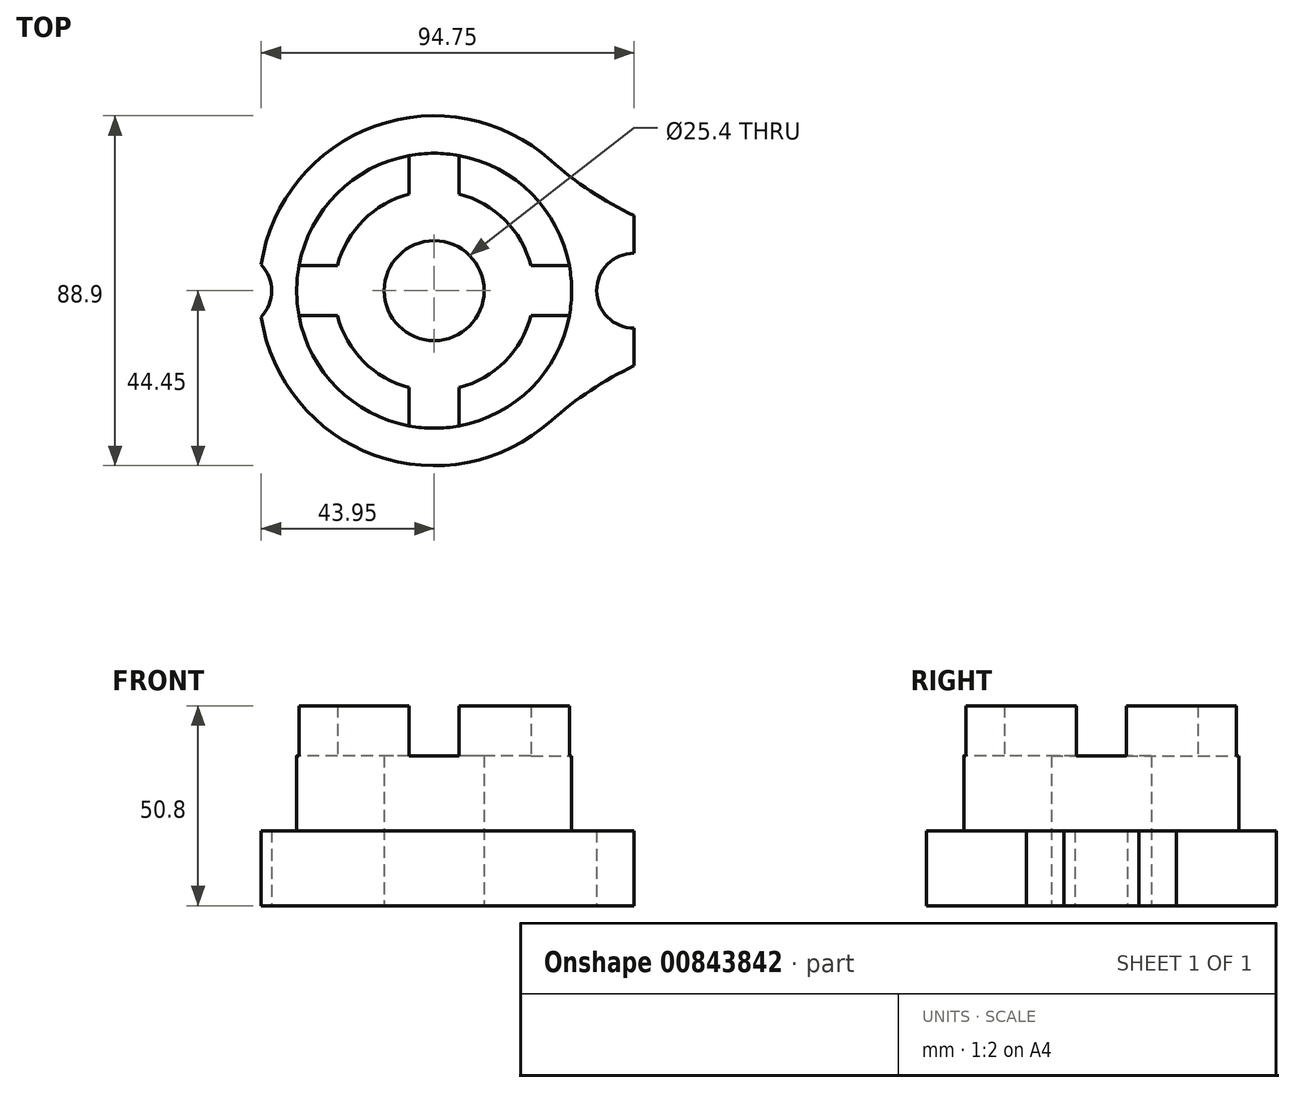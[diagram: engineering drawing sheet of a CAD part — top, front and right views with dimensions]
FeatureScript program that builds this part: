
annotation { "Feature Type Name" : "Feature", "Feature Type Description" : "" }
export const myFeature = defineFeature(function(context is Context, id is Id, definition is map)
    precondition{}
    {
        {
            var Q0;
            Q0=qCreatedBy(makeId("Top.planeOp"),FACE);
            var sketch = newSketch(context, id + "F0", { "sketchPlane" : qUnion([Q0])});
            skCircle(sketch, "E0", {"center": v(0, 0) * mm, "radius": 12.7 * mm});
            skCircle(sketch, "E1", {"center": v(0, 0) * mm, "radius": 25.4 * mm});
            skCircle(sketch, "E2", {"center": v(0, 0) * mm, "radius": 34.93 * mm});
            skLineSegment(sketch, "E3.top", {"start": v(0, -50.8) * mm, "end": v(50.8, -50.8) * mm});
            skLineSegment(sketch, "E4.top", {"start": v(0, 50.8) * mm, "end": v(50.8, 50.8) * mm});
            skLineSegment(sketch, "E5.bottom", {"start": v(50.8, 50.8) * mm, "end": v(-50.8, 50.8) * mm});
            skLineSegment(sketch, "E5.top", {"start": v(50.8, -50.8) * mm, "end": v(-50.8, -50.8) * mm});
            skLineSegment(sketch, "E5.right", {"start": v(-50.8, 50.8) * mm, "end": v(-50.8, -50.8) * mm});
            skLineSegment(sketch, "E6", {"start": v(50.8, 50.8) * mm, "end": v(50.8, -50.8) * mm});
            skLineSegment(sketch, "E7", {"start": v(-6.35, -24.6) * mm, "end": v(-6.35, -34.34) * mm});
            skLineSegment(sketch, "E8", {"start": v(6.35, -24.6) * mm, "end": v(6.35, -34.34) * mm});
            skLineSegment(sketch, "E9", {"start": v(24.6, -6.35) * mm, "end": v(34.34, -6.35) * mm});
            skLineSegment(sketch, "E10", {"start": v(24.6, 6.35) * mm, "end": v(34.34, 6.35) * mm});
            skLineSegment(sketch, "E11", {"start": v(-6.35, 24.6) * mm, "end": v(-6.35, 34.34) * mm});
            skLineSegment(sketch, "E12", {"start": v(6.35, 24.6) * mm, "end": v(6.35, 34.34) * mm});
            skLineSegment(sketch, "E13", {"start": v(-24.6, 6.35) * mm, "end": v(-34.34, 6.35) * mm});
            skLineSegment(sketch, "E14", {"start": v(-24.6, -6.35) * mm, "end": v(-34.34, -6.35) * mm});
            skCircle(sketch, "E15", {"center": v(50.8, 0) * mm, "radius": 9.53 * mm});
            skCircle(sketch, "E16", {"center": v(-50.8, 0) * mm, "radius": 9.53 * mm});
            skCircle(sketch, "E17", {"center": v(0, 0) * mm, "radius": 44.45 * mm});
            skCircle(sketch, "E18", {"center": v(-50.8, 0) * mm, "radius": 19.05 * mm});
            skCircle(sketch, "E19", {"center": v(50.8, 0) * mm, "radius": 19.05 * mm});
            skSolve(sketch);
        }
        {
            var Q0;
            {var subQ0=sQuery(id+"F0.wireOp",EDGE,"E5.right");var subQ1=sQuery(id+"F0.wireOp",EDGE,"E16");var subQ2=makeQuery(id+"F0.imprint","INTERSECT",VERTEX,{"disambiguationData":[OD(1.0)],"derivedFrom":[subQ1,subQ0]});Q0=makeQuery(id+"F0.imprint","IMPRINT",FACE,{"disambiguationData":[TD([[makeQuery(id+"F0.imprint","IMPRINT",EDGE,{"disambiguationData":[TD([[subQ2,-1.0]])],"derivedFrom":subQ1}),-1.0]])]});}
            var Q1;
            {var subQ5=sQuery(id+"F0.wireOp",EDGE,"E2");var subQ8=makeQuery(id+"F0.imprint","INTERSECT",VERTEX,{"derivedFrom":[subQ5,sQuery(id+"F0.wireOp",EDGE,"E7")]});Q1=makeQuery(id+"F0.imprint","IMPRINT",FACE,{"disambiguationData":[TD([[makeQuery(id+"F0.imprint","IMPRINT",EDGE,{"disambiguationData":[TD([[subQ8,1.0]])],"derivedFrom":subQ5}),-1.0]])]});}
            var Q2;
            {var subQ7=sQuery(id+"F0.wireOp",EDGE,"E12");Q2=makeQuery(id+"F0.imprint","IMPRINT",FACE,{"disambiguationData":[TD([[makeQuery(id+"F0.imprint","IMPRINT",EDGE,{"derivedFrom":subQ7}),-1.0]])]});}
            var Q3;
            {var subQ0=sQuery(id+"F0.wireOp",EDGE,"E17");var subQ1=sQuery(id+"F0.wireOp",EDGE,"E15");var subQ2=makeQuery(id+"F0.imprint","INTERSECT",VERTEX,{"disambiguationData":[OD(0.0)],"derivedFrom":[subQ1,subQ0]});Q3=makeQuery(id+"F0.imprint","IMPRINT",FACE,{"disambiguationData":[TD([[makeQuery(id+"F0.imprint","IMPRINT",EDGE,{"disambiguationData":[TD([[subQ2,1.0]])],"derivedFrom":subQ1}),-1.0]])]});}
            var Q4;
            {var subQ0=sQuery(id+"F0.wireOp",EDGE,"E5.right");var subQ1=sQuery(id+"F0.wireOp",EDGE,"E16");var subQ2=makeQuery(id+"F0.imprint","INTERSECT",VERTEX,{"disambiguationData":[OD(0.0)],"derivedFrom":[subQ1,subQ0]});Q4=makeQuery(id+"F0.imprint","IMPRINT",FACE,{"disambiguationData":[TD([[makeQuery(id+"F0.imprint","IMPRINT",EDGE,{"disambiguationData":[TD([[subQ2,1.0]])],"derivedFrom":subQ1}),-1.0]])]});}
            var Q5;
            {var subQ0=sQuery(id+"F0.wireOp",EDGE,"E13");var subQ1=sQuery(id+"F0.wireOp",EDGE,"E1");var subQ2=makeQuery(id+"F0.imprint","INTERSECT",VERTEX,{"derivedFrom":[subQ1,subQ0]});Q5=makeQuery(id+"F0.imprint","IMPRINT",FACE,{"disambiguationData":[TD([[makeQuery(id+"F0.imprint","IMPRINT",EDGE,{"disambiguationData":[TD([[subQ2,-1.0]])],"derivedFrom":subQ1}),-1.0]])]});}
            var Q6;
            {var subQ4=sQuery(id+"F0.wireOp",EDGE,"E2");var subQ8=makeQuery(id+"F0.imprint","INTERSECT",VERTEX,{"derivedFrom":[subQ4,sQuery(id+"F0.wireOp",EDGE,"E13")]});Q6=makeQuery(id+"F0.imprint","IMPRINT",FACE,{"disambiguationData":[TD([[makeQuery(id+"F0.imprint","IMPRINT",EDGE,{"disambiguationData":[TD([[subQ8,1.0]])],"derivedFrom":subQ4}),-1.0]])]});}
            var Q7;
            {var subQ0=sQuery(id+"F0.wireOp",EDGE,"E5.right");var subQ1=sQuery(id+"F0.wireOp",EDGE,"E16");var subQ2=makeQuery(id+"F0.imprint","INTERSECT",VERTEX,{"disambiguationData":[OD(0.0)],"derivedFrom":[subQ1,subQ0]});Q7=makeQuery(id+"F0.imprint","IMPRINT",FACE,{"disambiguationData":[TD([[makeQuery(id+"F0.imprint","IMPRINT",EDGE,{"disambiguationData":[TD([[subQ2,1.0]])],"derivedFrom":subQ1}),1.0]])]});}
            var Q8;
            {var subQ0=sQuery(id+"F0.wireOp",EDGE,"E17");var subQ1=sQuery(id+"F0.wireOp",EDGE,"E16");var subQ2=makeQuery(id+"F0.imprint","INTERSECT",VERTEX,{"disambiguationData":[OD(0.0)],"derivedFrom":[subQ1,subQ0]});Q8=makeQuery(id+"F0.imprint","IMPRINT",FACE,{"disambiguationData":[TD([[makeQuery(id+"F0.imprint","IMPRINT",EDGE,{"disambiguationData":[TD([[subQ2,1.0]])],"derivedFrom":subQ1}),1.0]])]});}
            var Q9;
            {var subQ0=sQuery(id+"F0.wireOp",EDGE,"E9");var subQ1=sQuery(id+"F0.wireOp",EDGE,"E2");var subQ2=makeQuery(id+"F0.imprint","INTERSECT",VERTEX,{"derivedFrom":[subQ1,subQ0]});Q9=makeQuery(id+"F0.imprint","IMPRINT",FACE,{"disambiguationData":[TD([[makeQuery(id+"F0.imprint","IMPRINT",EDGE,{"disambiguationData":[TD([[subQ2,-1.0]])],"derivedFrom":subQ1}),1.0]])]});}
            var Q10;
            Q10=makeQuery(id+"F0.imprint","IMPRINT",FACE,{"disambiguationData":[TD([[makeQuery(id+"F0.imprint","IMPRINT",EDGE,{"derivedFrom":sQuery(id+"F0.wireOp",EDGE,"E0")}),-1.0]])]});
            var Q11;
            {var subQ0=sQuery(id+"F0.wireOp",EDGE,"E7");Q11=makeQuery(id+"F0.imprint","IMPRINT",FACE,{"disambiguationData":[TD([[makeQuery(id+"F0.imprint","IMPRINT",EDGE,{"derivedFrom":subQ0}),1.0]])]});}
            var Q12;
            {var subQ0=sQuery(id+"F0.wireOp",EDGE,"E11");Q12=makeQuery(id+"F0.imprint","IMPRINT",FACE,{"disambiguationData":[TD([[makeQuery(id+"F0.imprint","IMPRINT",EDGE,{"derivedFrom":subQ0}),-1.0]])]});}
            var Q13;
            {var subQ0=sQuery(id+"F0.wireOp",EDGE,"E6");var subQ1=sQuery(id+"F0.wireOp",EDGE,"E15");var subQ2=makeQuery(id+"F0.imprint","INTERSECT",VERTEX,{"disambiguationData":[OD(0.0)],"derivedFrom":[subQ1,subQ0]});Q13=makeQuery(id+"F0.imprint","IMPRINT",FACE,{"disambiguationData":[TD([[makeQuery(id+"F0.imprint","IMPRINT",EDGE,{"disambiguationData":[TD([[subQ2,1.0]])],"derivedFrom":subQ1}),-1.0]])]});}
            var Q14;
            {var subQ5=sQuery(id+"F0.wireOp",EDGE,"E11");Q14=makeQuery(id+"F0.imprint","IMPRINT",FACE,{"disambiguationData":[TD([[makeQuery(id+"F0.imprint","IMPRINT",EDGE,{"derivedFrom":subQ5}),1.0]])]});}
            var Q15;
            {var subQ5=sQuery(id+"F0.wireOp",EDGE,"E7");Q15=makeQuery(id+"F0.imprint","IMPRINT",FACE,{"disambiguationData":[TD([[makeQuery(id+"F0.imprint","IMPRINT",EDGE,{"derivedFrom":subQ5}),-1.0]])]});}
            var Q16;
            {var subQ0=sQuery(id+"F0.wireOp",EDGE,"E5.right");var subQ1=sQuery(id+"F0.wireOp",EDGE,"E16");var subQ2=makeQuery(id+"F0.imprint","INTERSECT",VERTEX,{"disambiguationData":[OD(0.0)],"derivedFrom":[subQ1,subQ0]});Q16=makeQuery(id+"F0.imprint","IMPRINT",FACE,{"disambiguationData":[TD([[makeQuery(id+"F0.imprint","IMPRINT",EDGE,{"disambiguationData":[TD([[subQ2,-1.0]])],"derivedFrom":subQ1}),1.0]])]});}
            var Q17;
            {var subQ0=sQuery(id+"F0.wireOp",EDGE,"E5.right");var subQ1=sQuery(id+"F0.wireOp",EDGE,"E16");var subQ2=makeQuery(id+"F0.imprint","INTERSECT",VERTEX,{"disambiguationData":[OD(0.0)],"derivedFrom":[subQ1,subQ0]});Q17=makeQuery(id+"F0.imprint","IMPRINT",FACE,{"disambiguationData":[TD([[makeQuery(id+"F0.imprint","IMPRINT",EDGE,{"disambiguationData":[TD([[subQ2,-1.0]])],"derivedFrom":subQ1}),-1.0]])]});}
            var Q18;
            {var subQ0=sQuery(id+"F0.wireOp",EDGE,"E13");var subQ1=sQuery(id+"F0.wireOp",EDGE,"E2");var subQ2=makeQuery(id+"F0.imprint","INTERSECT",VERTEX,{"derivedFrom":[subQ1,subQ0]});Q18=makeQuery(id+"F0.imprint","IMPRINT",FACE,{"disambiguationData":[TD([[makeQuery(id+"F0.imprint","IMPRINT",EDGE,{"disambiguationData":[TD([[subQ2,-1.0]])],"derivedFrom":subQ1}),1.0]])]});}
            var Q19;
            {var subQ0=sQuery(id+"F0.wireOp",EDGE,"E17");var subQ1=sQuery(id+"F0.wireOp",EDGE,"E15");var subQ2=makeQuery(id+"F0.imprint","INTERSECT",VERTEX,{"disambiguationData":[OD(0.0)],"derivedFrom":[subQ1,subQ0]});Q19=makeQuery(id+"F0.imprint","IMPRINT",FACE,{"disambiguationData":[TD([[makeQuery(id+"F0.imprint","IMPRINT",EDGE,{"disambiguationData":[TD([[subQ2,-1.0]])],"derivedFrom":subQ1}),1.0]])]});}
            var Q20;
            {var subQ5=sQuery(id+"F0.wireOp",EDGE,"E2");var subQ6=makeQuery(id+"F0.imprint","INTERSECT",VERTEX,{"derivedFrom":[subQ5,sQuery(id+"F0.wireOp",EDGE,"E12")]});Q20=makeQuery(id+"F0.imprint","IMPRINT",FACE,{"disambiguationData":[TD([[makeQuery(id+"F0.imprint","IMPRINT",EDGE,{"disambiguationData":[TD([[subQ6,1.0]])],"derivedFrom":subQ5}),-1.0]])]});}
            var Q21;
            {var subQ0=sQuery(id+"F0.wireOp",EDGE,"E17");var subQ1=sQuery(id+"F0.wireOp",EDGE,"E15");var subQ2=makeQuery(id+"F0.imprint","INTERSECT",VERTEX,{"disambiguationData":[OD(0.0)],"derivedFrom":[subQ1,subQ0]});Q21=makeQuery(id+"F0.imprint","IMPRINT",FACE,{"disambiguationData":[TD([[makeQuery(id+"F0.imprint","IMPRINT",EDGE,{"disambiguationData":[TD([[subQ2,1.0]])],"derivedFrom":subQ1}),1.0]])]});}
            var Q22;
            {var subQ0=sQuery(id+"F0.wireOp",EDGE,"E6");var subQ1=sQuery(id+"F0.wireOp",EDGE,"E15");var subQ2=makeQuery(id+"F0.imprint","INTERSECT",VERTEX,{"disambiguationData":[OD(0.0)],"derivedFrom":[subQ1,subQ0]});Q22=makeQuery(id+"F0.imprint","IMPRINT",FACE,{"disambiguationData":[TD([[makeQuery(id+"F0.imprint","IMPRINT",EDGE,{"disambiguationData":[TD([[subQ2,1.0]])],"derivedFrom":subQ1}),1.0]])]});}
            var Q23;
            {var subQ0=sQuery(id+"F0.wireOp",EDGE,"E17");var subQ1=sQuery(id+"F0.wireOp",EDGE,"E15");var subQ2=makeQuery(id+"F0.imprint","INTERSECT",VERTEX,{"disambiguationData":[OD(1.0)],"derivedFrom":[subQ1,subQ0]});Q23=makeQuery(id+"F0.imprint","IMPRINT",FACE,{"disambiguationData":[TD([[makeQuery(id+"F0.imprint","IMPRINT",EDGE,{"disambiguationData":[TD([[subQ2,-1.0]])],"derivedFrom":subQ1}),-1.0]])]});}
            var Q24;
            {var subQ0=sQuery(id+"F0.wireOp",EDGE,"E9");var subQ1=sQuery(id+"F0.wireOp",EDGE,"E1");var subQ2=makeQuery(id+"F0.imprint","INTERSECT",VERTEX,{"derivedFrom":[subQ1,subQ0]});Q24=makeQuery(id+"F0.imprint","IMPRINT",FACE,{"disambiguationData":[TD([[makeQuery(id+"F0.imprint","IMPRINT",EDGE,{"disambiguationData":[TD([[subQ2,-1.0]])],"derivedFrom":subQ1}),-1.0]])]});}
            var Q25;
            {var subQ4=sQuery(id+"F0.wireOp",EDGE,"E2");var subQ6=makeQuery(id+"F0.imprint","INTERSECT",VERTEX,{"derivedFrom":[subQ4,sQuery(id+"F0.wireOp",EDGE,"E10")]});Q25=makeQuery(id+"F0.imprint","IMPRINT",FACE,{"disambiguationData":[TD([[makeQuery(id+"F0.imprint","IMPRINT",EDGE,{"disambiguationData":[TD([[subQ6,-1.0]])],"derivedFrom":subQ4}),-1.0]])]});}
            var Q26;
            {var subQ5=sQuery(id+"F0.wireOp",EDGE,"E8");Q26=makeQuery(id+"F0.imprint","IMPRINT",FACE,{"disambiguationData":[TD([[makeQuery(id+"F0.imprint","IMPRINT",EDGE,{"derivedFrom":subQ5}),1.0]])]});}
            var Q27;
            {var subQ0=sQuery(id+"F0.wireOp",EDGE,"E14");var subQ1=sQuery(id+"F0.wireOp",EDGE,"E2");var subQ2=makeQuery(id+"F0.imprint","INTERSECT",VERTEX,{"derivedFrom":[subQ1,subQ0]});Q27=makeQuery(id+"F0.imprint","IMPRINT",FACE,{"disambiguationData":[TD([[makeQuery(id+"F0.imprint","IMPRINT",EDGE,{"disambiguationData":[TD([[subQ2,-1.0]])],"derivedFrom":subQ1}),1.0]])]});}
            var Q28;
            {var subQ0=sQuery(id+"F0.wireOp",EDGE,"E10");var subQ1=sQuery(id+"F0.wireOp",EDGE,"E2");var subQ2=makeQuery(id+"F0.imprint","INTERSECT",VERTEX,{"derivedFrom":[subQ1,subQ0]});Q28=makeQuery(id+"F0.imprint","IMPRINT",FACE,{"disambiguationData":[TD([[makeQuery(id+"F0.imprint","IMPRINT",EDGE,{"disambiguationData":[TD([[subQ2,-1.0]])],"derivedFrom":subQ1}),1.0]])]});}
            var Q29;
            {var subQ0=sQuery(id+"F0.wireOp",EDGE,"E9");var subQ1=sQuery(id+"F0.wireOp",EDGE,"E2");var subQ2=makeQuery(id+"F0.imprint","INTERSECT",VERTEX,{"derivedFrom":[subQ1,subQ0]});Q29=makeQuery(id+"F0.imprint","IMPRINT",FACE,{"disambiguationData":[TD([[makeQuery(id+"F0.imprint","IMPRINT",EDGE,{"disambiguationData":[TD([[subQ2,1.0]])],"derivedFrom":subQ1}),1.0]])]});}
            var Q30;
            {var subQ0=sQuery(id+"F0.wireOp",EDGE,"E13");var subQ1=sQuery(id+"F0.wireOp",EDGE,"E2");var subQ2=makeQuery(id+"F0.imprint","INTERSECT",VERTEX,{"derivedFrom":[subQ1,subQ0]});Q30=makeQuery(id+"F0.imprint","IMPRINT",FACE,{"disambiguationData":[TD([[makeQuery(id+"F0.imprint","IMPRINT",EDGE,{"disambiguationData":[TD([[subQ2,1.0]])],"derivedFrom":subQ1}),1.0]])]});}
            extrude(context, id + "F1", {"entities" : qUnion([Q0, Q1, Q2, Q3, Q4, Q5, Q6, Q7, Q8, Q9, Q10, Q11, Q12, Q13, Q14, Q15, Q16, Q17, Q18, Q19, Q20, Q21, Q22, Q23, Q24, Q25, Q26, Q27, Q28, Q29, Q30]), "depth" : 19.05 * mm, "offsetDistance" : 25.4 * mm});
        }
        {
            var Q0;
            {var subQ0=sQuery(id+"F0.wireOp",EDGE,"E13");Q0=makeQuery(id+"F0.imprint","IMPRINT",FACE,{"disambiguationData":[TD([[makeQuery(id+"F0.imprint","IMPRINT",EDGE,{"derivedFrom":subQ0}),1.0]])]});}
            var Q1;
            {var subQ0=sQuery(id+"F0.wireOp",EDGE,"E7");Q1=makeQuery(id+"F0.imprint","IMPRINT",FACE,{"disambiguationData":[TD([[makeQuery(id+"F0.imprint","IMPRINT",EDGE,{"derivedFrom":subQ0}),1.0]])]});}
            var Q2;
            {var subQ0=sQuery(id+"F0.wireOp",EDGE,"E11");Q2=makeQuery(id+"F0.imprint","IMPRINT",FACE,{"disambiguationData":[TD([[makeQuery(id+"F0.imprint","IMPRINT",EDGE,{"derivedFrom":subQ0}),-1.0]])]});}
            var Q3;
            {var subQ0=sQuery(id+"F0.wireOp",EDGE,"E9");Q3=makeQuery(id+"F0.imprint","IMPRINT",FACE,{"disambiguationData":[TD([[makeQuery(id+"F0.imprint","IMPRINT",EDGE,{"derivedFrom":subQ0}),1.0]])]});}
            var Q4;
            Q4=makeQuery(id+"F0.imprint","IMPRINT",FACE,{"disambiguationData":[TD([[makeQuery(id+"F0.imprint","IMPRINT",EDGE,{"derivedFrom":sQuery(id+"F0.wireOp",EDGE,"E0")}),-1.0]])]});
            var Q5;
            {var subQ0=sQuery(id+"F0.wireOp",EDGE,"E10");var subQ1=sQuery(id+"F0.wireOp",EDGE,"E2");var subQ2=makeQuery(id+"F0.imprint","INTERSECT",VERTEX,{"derivedFrom":[subQ1,subQ0]});Q5=makeQuery(id+"F0.imprint","IMPRINT",FACE,{"disambiguationData":[TD([[makeQuery(id+"F0.imprint","IMPRINT",EDGE,{"disambiguationData":[TD([[subQ2,-1.0]])],"derivedFrom":subQ1}),1.0]])]});}
            var Q6;
            {var subQ0=sQuery(id+"F0.wireOp",EDGE,"E9");var subQ1=sQuery(id+"F0.wireOp",EDGE,"E2");var subQ2=makeQuery(id+"F0.imprint","INTERSECT",VERTEX,{"derivedFrom":[subQ1,subQ0]});Q6=makeQuery(id+"F0.imprint","IMPRINT",FACE,{"disambiguationData":[TD([[makeQuery(id+"F0.imprint","IMPRINT",EDGE,{"disambiguationData":[TD([[subQ2,1.0]])],"derivedFrom":subQ1}),1.0]])]});}
            var Q7;
            {var subQ0=sQuery(id+"F0.wireOp",EDGE,"E14");var subQ1=sQuery(id+"F0.wireOp",EDGE,"E2");var subQ2=makeQuery(id+"F0.imprint","INTERSECT",VERTEX,{"derivedFrom":[subQ1,subQ0]});Q7=makeQuery(id+"F0.imprint","IMPRINT",FACE,{"disambiguationData":[TD([[makeQuery(id+"F0.imprint","IMPRINT",EDGE,{"disambiguationData":[TD([[subQ2,-1.0]])],"derivedFrom":subQ1}),1.0]])]});}
            var Q8;
            {var subQ0=sQuery(id+"F0.wireOp",EDGE,"E13");var subQ1=sQuery(id+"F0.wireOp",EDGE,"E2");var subQ2=makeQuery(id+"F0.imprint","INTERSECT",VERTEX,{"derivedFrom":[subQ1,subQ0]});Q8=makeQuery(id+"F0.imprint","IMPRINT",FACE,{"disambiguationData":[TD([[makeQuery(id+"F0.imprint","IMPRINT",EDGE,{"disambiguationData":[TD([[subQ2,1.0]])],"derivedFrom":subQ1}),1.0]])]});}
            extrude(context, id + "F2", {"entities" : qUnion([Q0, Q1, Q2, Q3, Q4, Q5, Q6, Q7, Q8]), "operationType" : NewBodyOperationType.ADD, "depth" : 38.1 * mm, "offsetDistance" : 25.4 * mm});
        }
        {
            var Q0;
            {var subQ5=sQuery(id+"F0.wireOp",EDGE,"E7");Q0=makeQuery(id+"F0.imprint","IMPRINT",FACE,{"disambiguationData":[TD([[makeQuery(id+"F0.imprint","IMPRINT",EDGE,{"derivedFrom":subQ5}),-1.0]])]});}
            var Q1;
            {var subQ5=sQuery(id+"F0.wireOp",EDGE,"E8");Q1=makeQuery(id+"F0.imprint","IMPRINT",FACE,{"disambiguationData":[TD([[makeQuery(id+"F0.imprint","IMPRINT",EDGE,{"derivedFrom":subQ5}),1.0]])]});}
            var Q2;
            {var subQ7=sQuery(id+"F0.wireOp",EDGE,"E12");Q2=makeQuery(id+"F0.imprint","IMPRINT",FACE,{"disambiguationData":[TD([[makeQuery(id+"F0.imprint","IMPRINT",EDGE,{"derivedFrom":subQ7}),-1.0]])]});}
            var Q3;
            {var subQ5=sQuery(id+"F0.wireOp",EDGE,"E11");Q3=makeQuery(id+"F0.imprint","IMPRINT",FACE,{"disambiguationData":[TD([[makeQuery(id+"F0.imprint","IMPRINT",EDGE,{"derivedFrom":subQ5}),1.0]])]});}
            var Q4;
            {var subQ0=sQuery(id+"F0.wireOp",EDGE,"E14");var subQ1=sQuery(id+"F0.wireOp",EDGE,"E2");var subQ2=makeQuery(id+"F0.imprint","INTERSECT",VERTEX,{"derivedFrom":[subQ1,subQ0]});Q4=makeQuery(id+"F0.imprint","IMPRINT",FACE,{"disambiguationData":[TD([[makeQuery(id+"F0.imprint","IMPRINT",EDGE,{"disambiguationData":[TD([[subQ2,-1.0]])],"derivedFrom":subQ1}),1.0]])]});}
            var Q5;
            {var subQ0=sQuery(id+"F0.wireOp",EDGE,"E13");var subQ1=sQuery(id+"F0.wireOp",EDGE,"E2");var subQ2=makeQuery(id+"F0.imprint","INTERSECT",VERTEX,{"derivedFrom":[subQ1,subQ0]});Q5=makeQuery(id+"F0.imprint","IMPRINT",FACE,{"disambiguationData":[TD([[makeQuery(id+"F0.imprint","IMPRINT",EDGE,{"disambiguationData":[TD([[subQ2,1.0]])],"derivedFrom":subQ1}),1.0]])]});}
            var Q6;
            {var subQ0=sQuery(id+"F0.wireOp",EDGE,"E9");var subQ1=sQuery(id+"F0.wireOp",EDGE,"E2");var subQ2=makeQuery(id+"F0.imprint","INTERSECT",VERTEX,{"derivedFrom":[subQ1,subQ0]});Q6=makeQuery(id+"F0.imprint","IMPRINT",FACE,{"disambiguationData":[TD([[makeQuery(id+"F0.imprint","IMPRINT",EDGE,{"disambiguationData":[TD([[subQ2,1.0]])],"derivedFrom":subQ1}),1.0]])]});}
            var Q7;
            {var subQ0=sQuery(id+"F0.wireOp",EDGE,"E10");var subQ1=sQuery(id+"F0.wireOp",EDGE,"E2");var subQ2=makeQuery(id+"F0.imprint","INTERSECT",VERTEX,{"derivedFrom":[subQ1,subQ0]});Q7=makeQuery(id+"F0.imprint","IMPRINT",FACE,{"disambiguationData":[TD([[makeQuery(id+"F0.imprint","IMPRINT",EDGE,{"disambiguationData":[TD([[subQ2,-1.0]])],"derivedFrom":subQ1}),1.0]])]});}
            extrude(context, id + "F3", {"entities" : qUnion([Q0, Q1, Q2, Q3, Q4, Q5, Q6, Q7]), "operationType" : NewBodyOperationType.ADD, "depth" : 50.8 * mm, "offsetDistance" : 25.4 * mm});
        }
        {
            var Q0;
            {var subQ0=sQuery(id+"F0.wireOp",EDGE,"E19");var subQ1=sQuery(id+"F0.wireOp",EDGE,"E17");Q0=makeQuery(id+"F1.opExtrude","SWEPT_EDGE",EDGE,{"disambiguationData":[OSD([subQ1,subQ0]),TDD([makeQuery(id+"F0.imprint","INTERSECT",VERTEX,{"disambiguationData":[OD(1.0)],"derivedFrom":[subQ1,subQ0]})])]});}
            var Q1;
            {var subQ0=sQuery(id+"F0.wireOp",EDGE,"E19");var subQ1=sQuery(id+"F0.wireOp",EDGE,"E17");Q1=makeQuery(id+"F1.opExtrude","SWEPT_EDGE",EDGE,{"disambiguationData":[OSD([subQ1,subQ0]),TDD([makeQuery(id+"F0.imprint","INTERSECT",VERTEX,{"disambiguationData":[OD(0.0)],"derivedFrom":[subQ1,subQ0]})])]});}
            var Q2;
            {var subQ0=sQuery(id+"F0.wireOp",EDGE,"E18");var subQ1=sQuery(id+"F0.wireOp",EDGE,"E17");Q2=makeQuery(id+"F1.opExtrude","SWEPT_EDGE",EDGE,{"disambiguationData":[OSD([subQ1,subQ0]),TDD([makeQuery(id+"F0.imprint","INTERSECT",VERTEX,{"disambiguationData":[OD(0.0)],"derivedFrom":[subQ1,subQ0]})])]});}
            var Q3;
            {var subQ0=sQuery(id+"F0.wireOp",EDGE,"E18");var subQ1=sQuery(id+"F0.wireOp",EDGE,"E17");Q3=makeQuery(id+"F1.opExtrude","SWEPT_EDGE",EDGE,{"disambiguationData":[OSD([subQ1,subQ0]),TDD([makeQuery(id+"F0.imprint","INTERSECT",VERTEX,{"disambiguationData":[OD(1.0)],"derivedFrom":[subQ1,subQ0]})])]});}
            fillet(context, id + "F4", {"entities" : qUnion([Q0, Q1, Q2, Q3]), "radius" : 88.9 * mm, "tangentPropagation" : true, "allowEdgeOverflow" : false});
        }
        {
            var Q0;
            {var subQ0=sQuery(id+"F0.wireOp",EDGE,"E5.right");var subQ1=sQuery(id+"F0.wireOp",EDGE,"E16");var subQ2=makeQuery(id+"F0.imprint","INTERSECT",VERTEX,{"disambiguationData":[OD(0.0)],"derivedFrom":[subQ1,subQ0]});Q0=makeQuery(id+"F0.imprint","IMPRINT",FACE,{"disambiguationData":[TD([[makeQuery(id+"F0.imprint","IMPRINT",EDGE,{"disambiguationData":[TD([[subQ2,1.0]])],"derivedFrom":subQ1}),1.0]])]});}
            var Q1;
            {var subQ0=sQuery(id+"F0.wireOp",EDGE,"E17");var subQ1=sQuery(id+"F0.wireOp",EDGE,"E16");var subQ2=makeQuery(id+"F0.imprint","INTERSECT",VERTEX,{"disambiguationData":[OD(0.0)],"derivedFrom":[subQ1,subQ0]});Q1=makeQuery(id+"F0.imprint","IMPRINT",FACE,{"disambiguationData":[TD([[makeQuery(id+"F0.imprint","IMPRINT",EDGE,{"disambiguationData":[TD([[subQ2,1.0]])],"derivedFrom":subQ1}),1.0]])]});}
            var Q2;
            {var subQ0=sQuery(id+"F0.wireOp",EDGE,"E5.right");var subQ1=sQuery(id+"F0.wireOp",EDGE,"E16");var subQ2=makeQuery(id+"F0.imprint","INTERSECT",VERTEX,{"disambiguationData":[OD(0.0)],"derivedFrom":[subQ1,subQ0]});Q2=makeQuery(id+"F0.imprint","IMPRINT",FACE,{"disambiguationData":[TD([[makeQuery(id+"F0.imprint","IMPRINT",EDGE,{"disambiguationData":[TD([[subQ2,-1.0]])],"derivedFrom":subQ1}),1.0]])]});}
            var Q3;
            {var subQ0=sQuery(id+"F0.wireOp",EDGE,"E17");var subQ1=sQuery(id+"F0.wireOp",EDGE,"E15");var subQ2=makeQuery(id+"F0.imprint","INTERSECT",VERTEX,{"disambiguationData":[OD(0.0)],"derivedFrom":[subQ1,subQ0]});Q3=makeQuery(id+"F0.imprint","IMPRINT",FACE,{"disambiguationData":[TD([[makeQuery(id+"F0.imprint","IMPRINT",EDGE,{"disambiguationData":[TD([[subQ2,-1.0]])],"derivedFrom":subQ1}),1.0]])]});}
            var Q4;
            {var subQ0=sQuery(id+"F0.wireOp",EDGE,"E17");var subQ1=sQuery(id+"F0.wireOp",EDGE,"E15");var subQ2=makeQuery(id+"F0.imprint","INTERSECT",VERTEX,{"disambiguationData":[OD(0.0)],"derivedFrom":[subQ1,subQ0]});Q4=makeQuery(id+"F0.imprint","IMPRINT",FACE,{"disambiguationData":[TD([[makeQuery(id+"F0.imprint","IMPRINT",EDGE,{"disambiguationData":[TD([[subQ2,1.0]])],"derivedFrom":subQ1}),1.0]])]});}
            var Q5;
            {var subQ0=sQuery(id+"F0.wireOp",EDGE,"E6");var subQ1=sQuery(id+"F0.wireOp",EDGE,"E15");var subQ2=makeQuery(id+"F0.imprint","INTERSECT",VERTEX,{"disambiguationData":[OD(0.0)],"derivedFrom":[subQ1,subQ0]});Q5=makeQuery(id+"F0.imprint","IMPRINT",FACE,{"disambiguationData":[TD([[makeQuery(id+"F0.imprint","IMPRINT",EDGE,{"disambiguationData":[TD([[subQ2,1.0]])],"derivedFrom":subQ1}),1.0]])]});}
            extrude(context, id + "F5", {"entities" : qUnion([Q0, Q1, Q2, Q3, Q4, Q5]), "operationType" : NewBodyOperationType.REMOVE, "depth" : 25.4 * mm, "offsetDistance" : 25.4 * mm});
        }
    });
